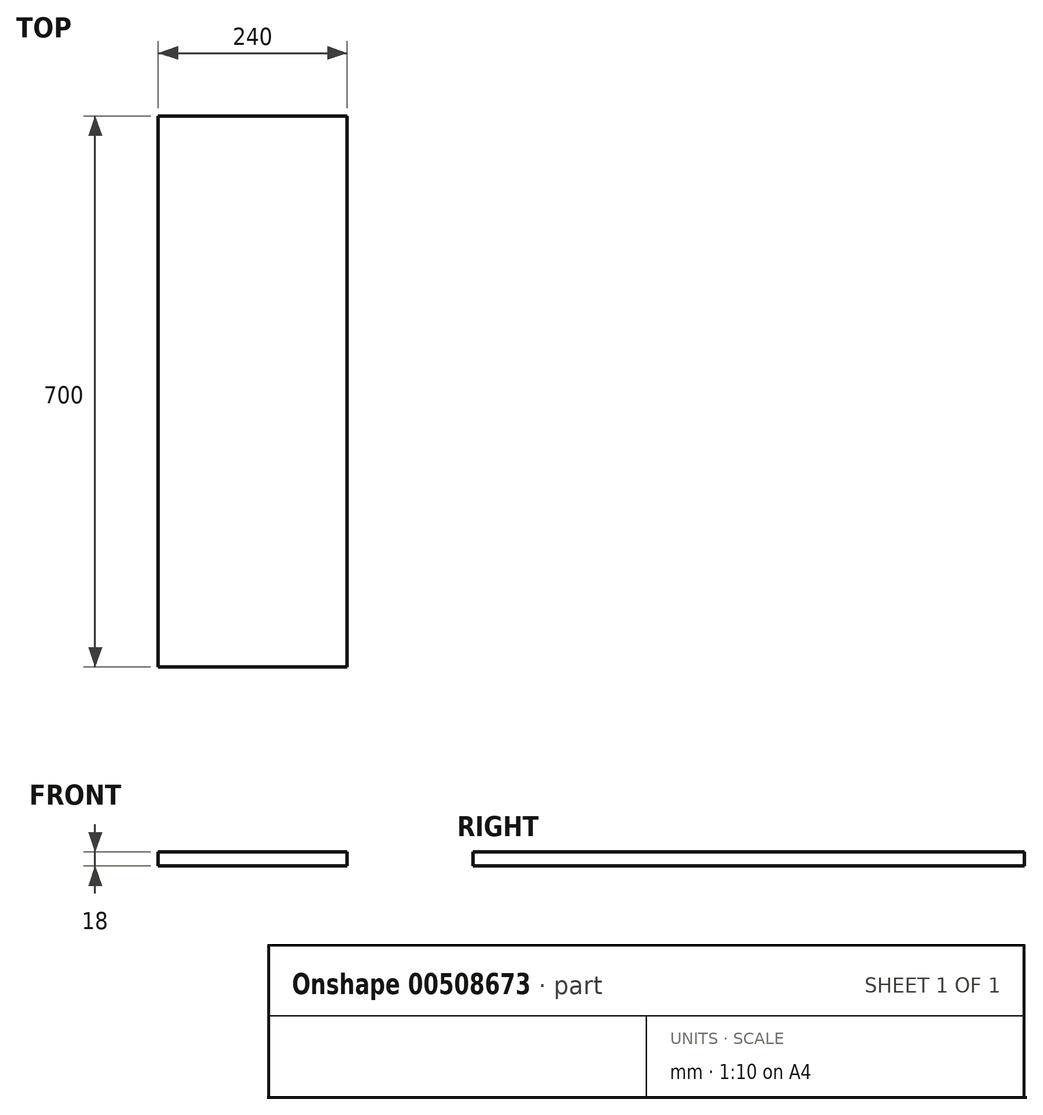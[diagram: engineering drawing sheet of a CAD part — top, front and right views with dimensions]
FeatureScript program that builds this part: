
annotation { "Feature Type Name" : "Feature", "Feature Type Description" : "" }
export const myFeature = defineFeature(function(context is Context, id is Id, definition is map)
    precondition{}
    {
        {
            var Q0;
            Q0=qCreatedBy(makeId("Top.planeOp"),FACE);
            var sketch = newSketch(context, id + "F0", { "sketchPlane" : qUnion([Q0])});
            skLineSegment(sketch, "E0.bottom", {"start": v(120, -350) * mm, "end": v(-120, -350) * mm});
            skLineSegment(sketch, "E0.top", {"start": v(120, 350) * mm, "end": v(-120, 350) * mm});
            skLineSegment(sketch, "E0.left", {"start": v(120, -350) * mm, "end": v(120, 350) * mm});
            skLineSegment(sketch, "E0.right", {"start": v(-120, -350) * mm, "end": v(-120, 350) * mm});
            skPoint(sketch, "E0.middle", {"position": v(0, 0) * mm});
            skSolve(sketch);
        }
        {
            var Q0;
            Q0=makeQuery(id+"F0.imprint","IMPRINT",FACE,{"disambiguationData":[TD([[makeQuery(id+"F0.imprint","IMPRINT",EDGE,{"derivedFrom":sQuery(id+"F0.wireOp",EDGE,"E0.bottom")}),-1.0]])]});
            extrude(context, id + "F1", {"entities" : qUnion([Q0]), "depth" : 18 * mm});
        }
    });
